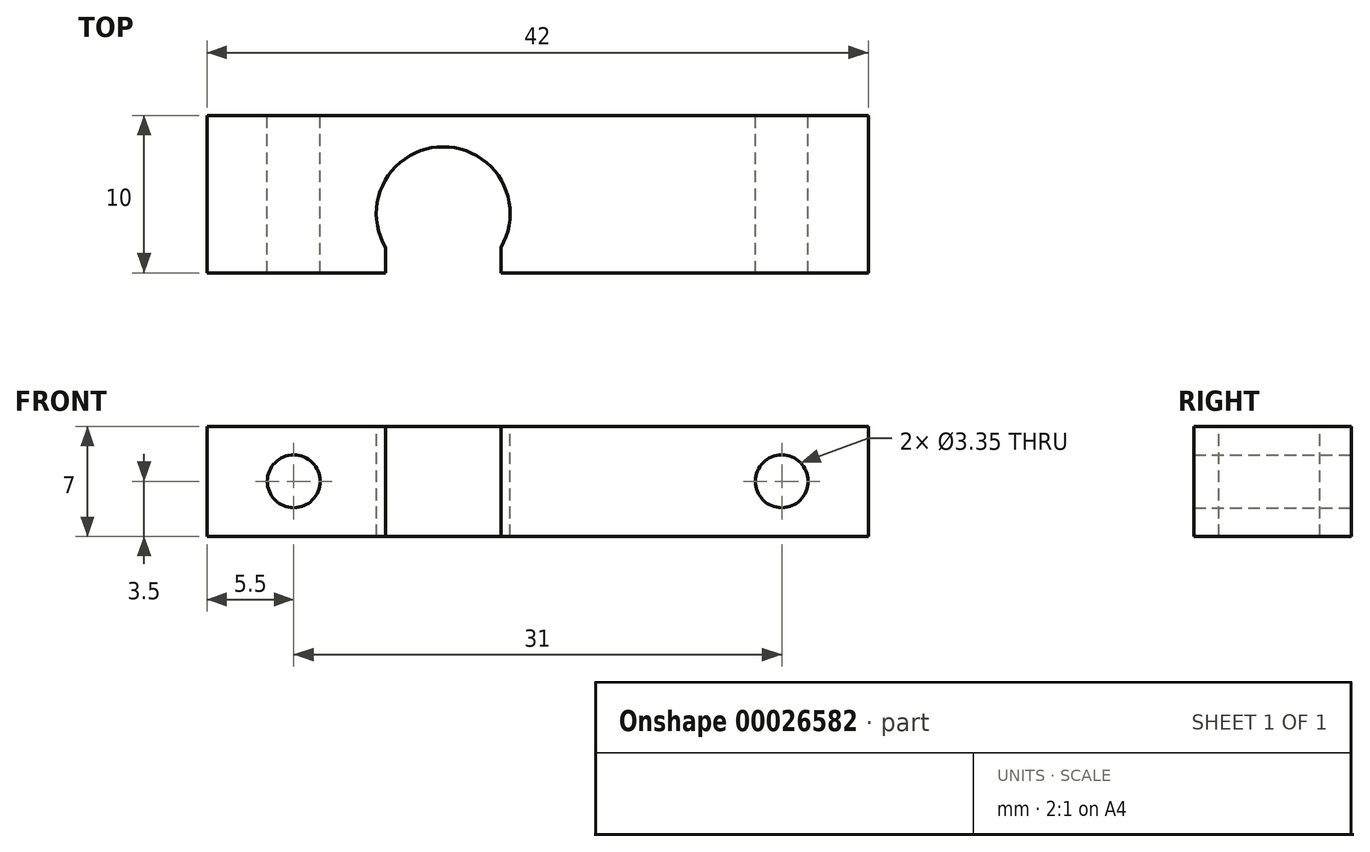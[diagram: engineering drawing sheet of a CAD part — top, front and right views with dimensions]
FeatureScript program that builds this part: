
annotation { "Feature Type Name" : "Feature", "Feature Type Description" : "" }
export const myFeature = defineFeature(function(context is Context, id is Id, definition is map)
    precondition{}
    {
        {
            var Q0;
            Q0=qCreatedBy(makeId("Top.planeOp"),FACE);
            var sketch = newSketch(context, id + "F0", { "sketchPlane" : qUnion([Q0])});
            skLineSegment(sketch, "E0.bottom", {"start": v(0, 0) * mm, "end": v(42, 0) * mm});
            skLineSegment(sketch, "E0.top", {"start": v(0, 10) * mm, "end": v(42, 10) * mm});
            skLineSegment(sketch, "E0.left", {"start": v(0, 0) * mm, "end": v(0, 10) * mm});
            skLineSegment(sketch, "E0.right", {"start": v(42, 0) * mm, "end": v(42, 10) * mm});
            skSolve(sketch);
        }
        {
            var Q0;
            Q0=qSketchRegion(id+"F0",true);
            extrude(context, id + "F1", {"entities" : qUnion([Q0]), "depth" : 7 * mm});
        }
        {
            var Q0;
            Q0=makeQuery(id+"F1.opExtrude","CAP_FACE",FACE,{"disambiguationData":[OSD([sQuery(id+"F0.wireOp",EDGE,"E0.bottom"),sQuery(id+"F0.wireOp",EDGE,"E0.top"),sQuery(id+"F0.wireOp",EDGE,"E0.left"),sQuery(id+"F0.wireOp",EDGE,"E0.right")])],"isStart":false});
            var sketch = newSketch(context, id + "F2", { "sketchPlane" : qUnion([Q0])});
            skCircle(sketch, "E1", {"center": v(15, 3.75) * mm, "radius": 4.25 * mm});
            skSolve(sketch);
        }
        {
            var Q0;
            Q0=qSketchRegion(id+"F2",true);
            extrude(context, id + "F3", {"entities" : qUnion([Q0]), "operationType" : NewBodyOperationType.REMOVE, "oppositeDirection" : true, "depth" : 25 * mm});
        }
        {
            var Q0;
            Q0=makeQuery(id+"F3.boolean.opBoolean","INTERSECT",EDGE,{"disambiguationData":[OD(0.0)],"derivedFrom":[makeQuery(id+"F1.opExtrude","SWEPT_FACE",FACE,{"disambiguationData":[OSD([sQuery(id+"F0.wireOp",EDGE,"E0.bottom")])]}),makeQuery(id+"F3.opExtrude","SWEPT_FACE",FACE,{"disambiguationData":[OSD([sQuery(id+"F2.wireOp",EDGE,"E1")])]})]});
            var Q1;
            Q1=makeQuery(id+"F3.boolean.opBoolean","INTERSECT",EDGE,{"disambiguationData":[OD(1.0)],"derivedFrom":[makeQuery(id+"F1.opExtrude","SWEPT_FACE",FACE,{"disambiguationData":[OSD([sQuery(id+"F0.wireOp",EDGE,"E0.bottom")])]}),makeQuery(id+"F3.opExtrude","SWEPT_FACE",FACE,{"disambiguationData":[OSD([sQuery(id+"F2.wireOp",EDGE,"E1")])]})]});
            chamfer(context, id + "F4", {"entities" : qUnion([Q0, Q1]), "chamferType" : ChamferType.OFFSET_ANGLE, "width" : 3 * mm, "oppositeDirection" : false, "angle" : 90 * degree, "tangentPropagation" : true});
        }
        {
            var Q0;
            Q0=makeQuery(id+"F1.opExtrude","SWEPT_FACE",FACE,{"disambiguationData":[OSD([sQuery(id+"F0.wireOp",EDGE,"E0.top")])]});
            var sketch = newSketch(context, id + "F5", { "sketchPlane" : qUnion([Q0])});
            skCircle(sketch, "E2", {"center": v(-5.5, 3.5) * mm, "radius": 1.68 * mm});
            skCircle(sketch, "E3", {"center": v(-36.5, 3.5) * mm, "radius": 1.68 * mm});
            skLineSegment(sketch, "E4", {"start": v(-5.5, 0) * mm, "end": v(-5.5, 7) * mm});
            skLineSegment(sketch, "E5", {"start": v(-5.5, 3.5) * mm, "end": v(0, 3.5) * mm});
            skLineSegment(sketch, "E6", {"start": v(-36.5, 3.5) * mm, "end": v(-42, 3.5) * mm});
            skSolve(sketch);
        }
        {
            var Q0;
            Q0=qSketchRegion(id+"F5",true);
            extrude(context, id + "F6", {"entities" : qUnion([Q0]), "operationType" : NewBodyOperationType.REMOVE, "oppositeDirection" : true, "depth" : 25 * mm});
        }
    });
